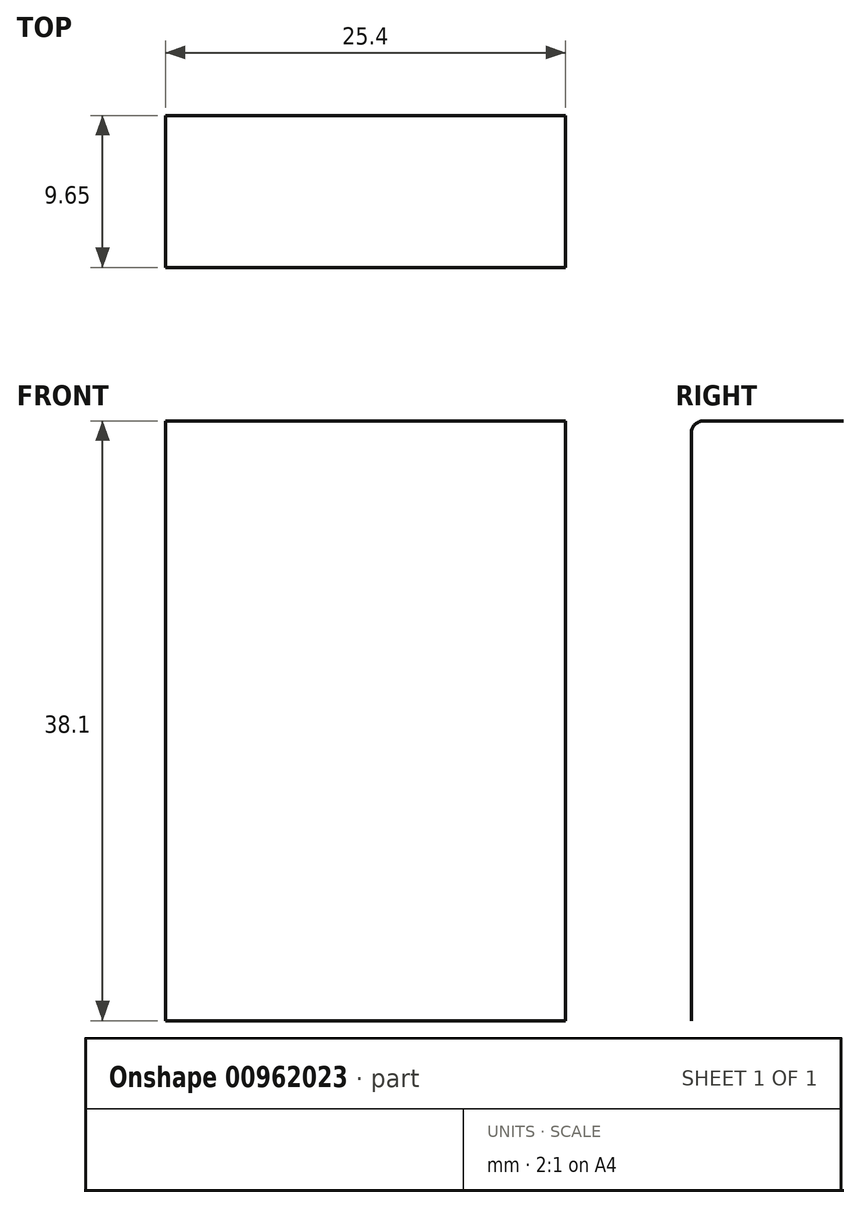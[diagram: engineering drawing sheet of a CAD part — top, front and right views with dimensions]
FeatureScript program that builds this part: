
annotation { "Feature Type Name" : "Feature", "Feature Type Description" : "" }
export const myFeature = defineFeature(function(context is Context, id is Id, definition is map)
    precondition{}
    {
        {
            var Q0;
            Q0=qCreatedBy(makeId("Right.planeOp"),FACE);
            var sketch = newSketch(context, id + "F0", { "sketchPlane" : qUnion([Q0])});
            skLineSegment(sketch, "E0", {"start": v(9.65, 38.1) * mm, "end": v(0.76, 38.1) * mm});
            skLineSegment(sketch, "E1", {"start": v(0, 0) * mm, "end": v(0, 37.34) * mm});
            skPoint(sketch, "E2.visualSharp", {"position": v(0, 38.1) * mm});
            skArc(sketch, "E2.filletArc", {"start": v(0.76, 38.1) * mm, "mid": v(0.22, 37.88) * mm, "end": v(0, 37.34) * mm});
            skLineSegment(sketch, "E3.0", {"start": v(0.38, 0) * mm, "end": v(0.38, 37.34) * mm});
            skLineSegment(sketch, "E4.0", {"start": v(9.65, 37.72) * mm, "end": v(0.76, 37.72) * mm});
            skArc(sketch, "E5.0", {"start": v(0.76, 37.72) * mm, "mid": v(0.5, 37.6) * mm, "end": v(0.38, 37.34) * mm});
            skLineSegment(sketch, "E6", {"start": v(0, 0) * mm, "end": v(0.38, 0) * mm});
            skSolve(sketch);
        }
        {
            var Q0;
            Q0=sQuery(id+"F0.wireOp",EDGE,"E1");
            var Q1;
            Q1=sQuery(id+"F0.wireOp",EDGE,"E2.filletArc");
            var Q2;
            Q2=sQuery(id+"F0.wireOp",EDGE,"E0");
            extrude(context, id + "F1", {"bodyType" : ToolBodyType.SURFACE, "surfaceEntities" : qUnion([Q0, Q1, Q2]), "depth" : 12.7 * mm, "offsetDistance" : 25.4 * mm, "hasSecondDirection" : true, "secondDirectionOppositeDirection" : true, "secondDirectionDepth" : 12.7 * mm});
        }
    });
